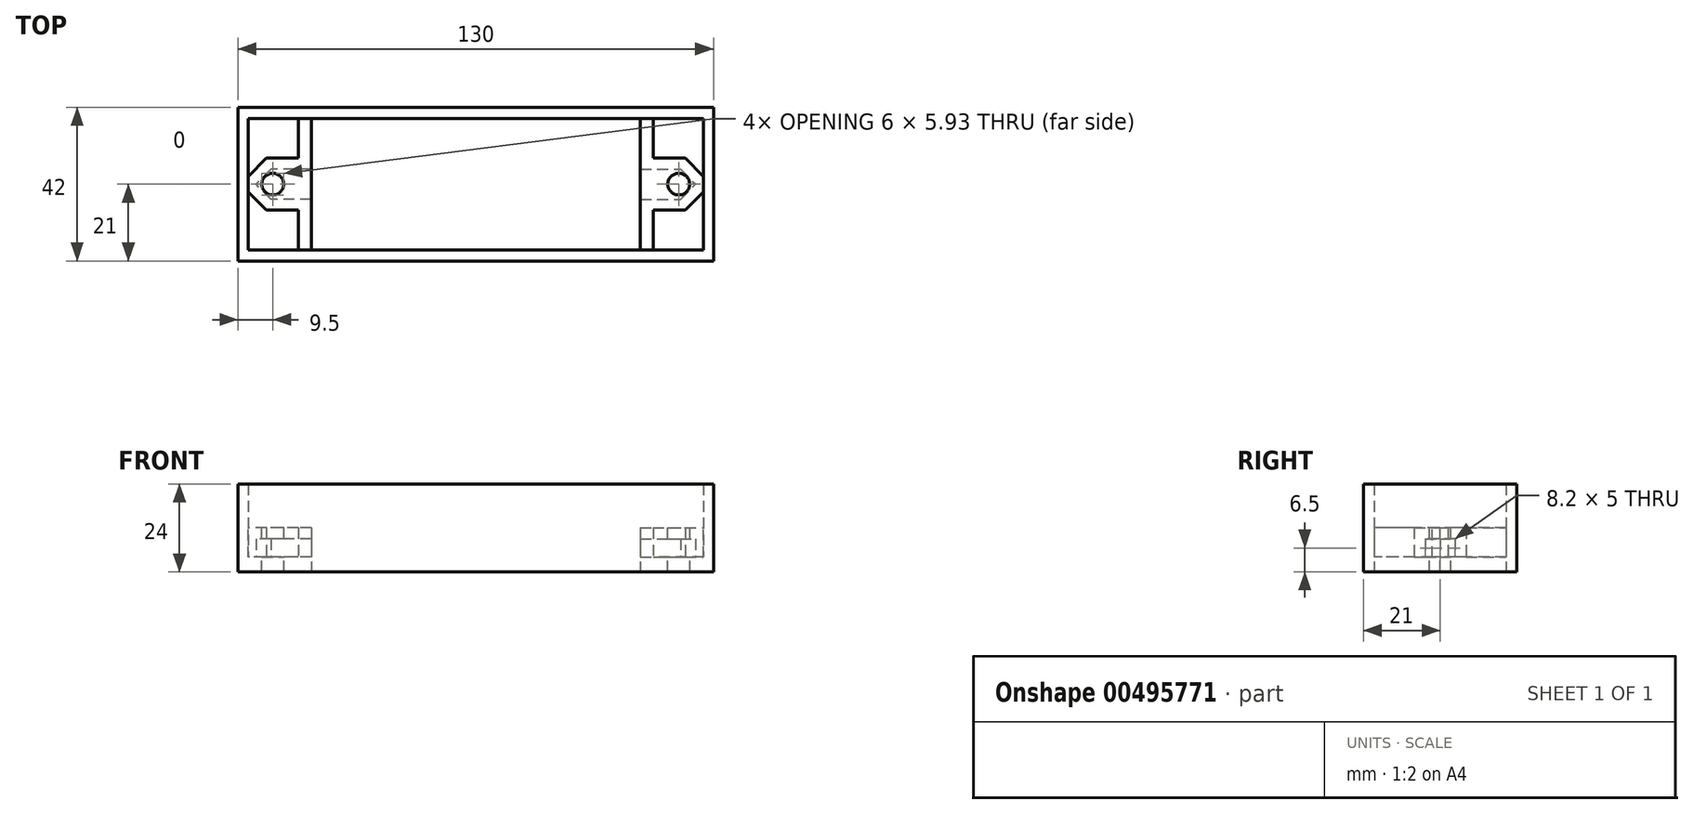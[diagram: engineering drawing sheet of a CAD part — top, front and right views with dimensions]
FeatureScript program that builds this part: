
annotation { "Feature Type Name" : "Feature", "Feature Type Description" : "" }
export const myFeature = defineFeature(function(context is Context, id is Id, definition is map)
    precondition{}
    {
        {
            var Q0;
            Q0=qCreatedBy(makeId("Top.planeOp"),FACE);
            var sketch = newSketch(context, id + "F0", { "sketchPlane" : qUnion([Q0])});
            skLineSegment(sketch, "E0.bottom", {"start": v(65, 21) * mm, "end": v(-65, 21) * mm});
            skLineSegment(sketch, "E0.top", {"start": v(65, -21) * mm, "end": v(-65, -21) * mm});
            skLineSegment(sketch, "E0.left", {"start": v(65, 21) * mm, "end": v(65, -21) * mm});
            skLineSegment(sketch, "E0.right", {"start": v(-65, 21) * mm, "end": v(-65, -21) * mm});
            skPoint(sketch, "E0.middle", {"position": v(0, 0) * mm});
            skLineSegment(sketch, "E1.bottom", {"start": v(-45, 18) * mm, "end": v(45, 18) * mm});
            skLineSegment(sketch, "E1.top", {"start": v(-45, -18) * mm, "end": v(45, -18) * mm});
            skLineSegment(sketch, "E1.left", {"start": v(-45, 18) * mm, "end": v(-45, -18) * mm});
            skLineSegment(sketch, "E1.right", {"start": v(45, 18) * mm, "end": v(45, -18) * mm});
            skSolve(sketch);
        }
        {
            var Q0;
            Q0 = qSketchRegion(id + "F0", true);
            extrude(context, id + "F1", {"entities" : qUnion([Q0]), "depth" : 4 * mm});
        }
        {
            var Q0;
            Q0=makeQuery(id+"F1.opExtrude","CAP_FACE",FACE,{"disambiguationData":[OSD([sQuery(id+"F0.wireOp",EDGE,"E0.bottom"),sQuery(id+"F0.wireOp",EDGE,"E0.top"),sQuery(id+"F0.wireOp",EDGE,"E0.left"),sQuery(id+"F0.wireOp",EDGE,"E0.right"),sQuery(id+"F0.wireOp",EDGE,"E1.bottom"),sQuery(id+"F0.wireOp",EDGE,"E1.top"),sQuery(id+"F0.wireOp",EDGE,"E1.left"),sQuery(id+"F0.wireOp",EDGE,"E1.right")])],"isStart":false});
            var sketch = newSketch(context, id + "F2", { "sketchPlane" : qUnion([Q0])});
            skLineSegment(sketch, "E2", {"start": v(45, 4.1) * mm, "end": v(56, 4.1) * mm});
            skLineSegment(sketch, "E3", {"start": v(56, 4.1) * mm, "end": v(60.1, 0) * mm});
            skLineSegment(sketch, "E4", {"start": v(60.1, 0) * mm, "end": v(45, 0) * mm});
            skLineSegment(sketch, "E5", {"start": v(45, 0) * mm, "end": v(45, 4.1) * mm});
            skLineSegment(sketch, "E6", {"start": v(56, 21) * mm, "end": v(56, -21) * mm, "construction": true});
            skLineSegment(sketch, "E7.MirrorCS", {"start": v(45, -4.1) * mm, "end": v(56, -4.1) * mm});
            skLineSegment(sketch, "E8.MirrorCS", {"start": v(56, -4.1) * mm, "end": v(60.1, 0) * mm});
            skLineSegment(sketch, "E9.MirrorCS", {"start": v(45, 0) * mm, "end": v(45, -4.1) * mm});
            skLineSegment(sketch, "E10.0", {"start": v(45, -7.1) * mm, "end": v(57.24, -7.1) * mm});
            skLineSegment(sketch, "E10.1", {"start": v(57.24, -7.1) * mm, "end": v(64.34, 0) * mm});
            skLineSegment(sketch, "E10.2", {"start": v(57.24, 7.1) * mm, "end": v(64.34, 0) * mm});
            skLineSegment(sketch, "E10.3", {"start": v(45, 7.1) * mm, "end": v(57.24, 7.1) * mm});
            skLineSegment(sketch, "E11.0", {"start": v(-60, -16) * mm, "end": v(60, -16) * mm, "construction": true});
            skLineSegment(sketch, "E11.1", {"start": v(-60, 16) * mm, "end": v(-60, -16) * mm, "construction": true});
            skLineSegment(sketch, "E11.2", {"start": v(60, 16) * mm, "end": v(-60, 16) * mm, "construction": true});
            skLineSegment(sketch, "E11.3", {"start": v(60, -16) * mm, "end": v(60, 16) * mm, "construction": true});
            skLineSegment(sketch, "E12.0", {"start": v(65, 21) * mm, "end": v(-60, 21) * mm});
            skLineSegment(sketch, "E12.1", {"start": v(65, -16) * mm, "end": v(65, 21) * mm});
            skSolve(sketch);
        }
        {
            var Q0;
            {var subQ1=sQuery(id+"F2.wireOp",EDGE,"E7.MirrorCS");Q0=makeQuery(id+"F2.imprint","IMPRINT",FACE,{"disambiguationData":[TD([[makeQuery(id+"F2.imprint","IMPRINT",EDGE,{"derivedFrom":subQ1}),-1.0]])]});}
            extrude(context, id + "F3", {"entities" : qUnion([Q0]), "operationType" : NewBodyOperationType.ADD, "depth" : 5 * mm});
        }
        {
            var Q0;
            Q0=makeQuery(id+"F3.opExtrude","CAP_FACE",FACE,{"disambiguationData":[OSD([sQuery(id+"F0.wireOp",EDGE,"E1.right"),sQuery(id+"F2.wireOp",EDGE,"E7.MirrorCS"),sQuery(id+"F2.wireOp",EDGE,"E8.MirrorCS"),sQuery(id+"F2.wireOp",EDGE,"E3"),sQuery(id+"F2.wireOp",EDGE,"E2"),sQuery(id+"F2.wireOp",EDGE,"E10.0"),sQuery(id+"F2.wireOp",EDGE,"E10.1"),sQuery(id+"F2.wireOp",EDGE,"E10.2"),sQuery(id+"F2.wireOp",EDGE,"E10.3")])],"isStart":false});
            var sketch = newSketch(context, id + "F4", { "sketchPlane" : qUnion([Q0])});
            skLineSegment(sketch, "E13", {"start": v(45, 7.1) * mm, "end": v(45, -7.1) * mm});
            skLineSegment(sketch, "E14", {"start": v(45, -7.1) * mm, "end": v(57.24, -7.1) * mm});
            skLineSegment(sketch, "E15", {"start": v(57.24, -7.1) * mm, "end": v(64.34, 0) * mm});
            skLineSegment(sketch, "E16", {"start": v(64.34, 0) * mm, "end": v(57.24, 7.1) * mm});
            skLineSegment(sketch, "E17", {"start": v(57.24, 7.1) * mm, "end": v(45, 7.1) * mm});
            skSolve(sketch);
        }
        {
            var Q0;
            {var subQ0=sQuery(id+"F4.wireOp",EDGE,"E14");Q0=makeQuery(id+"F4.imprint","IMPRINT",FACE,{"disambiguationData":[TD([[makeQuery(id+"F4.imprint","IMPRINT",EDGE,{"derivedFrom":subQ0}),1.0]])]});}
            var Q1;
            {var subQ0=makeQuery(id+"F3.opExtrude","CAP_EDGE",EDGE,{"disambiguationData":[OSD([sQuery(id+"F2.wireOp",EDGE,"E7.MirrorCS")])],"isStart":false});Q1=makeQuery(id+"F4.imprint","IMPRINT",FACE,{"disambiguationData":[TD([[makeQuery(id+"F4.imprint","IMPRINT",EDGE,{"derivedFrom":subQ0}),1.0]])]});}
            extrude(context, id + "F5", {"entities" : qUnion([Q0, Q1]), "operationType" : NewBodyOperationType.ADD, "depth" : 3 * mm});
        }
        {
            var Q0;
            Q0=makeQuery(id+"F5.boolean.opBoolean","MERGE",EDGE,{"derivedFrom":[makeQuery(id+"F3.opExtrude","SWEPT_EDGE",EDGE,{"disambiguationData":[OSD([sQuery(id+"F2.wireOp",EDGE,"E10.1"),sQuery(id+"F2.wireOp",EDGE,"E10.2")])]}),makeQuery(id+"F5.opExtrude","SWEPT_EDGE",EDGE,{"disambiguationData":[OSD([sQuery(id+"F4.wireOp",EDGE,"E15"),sQuery(id+"F4.wireOp",EDGE,"E16")])]})]});
            chamfer(context, id + "F6", {"entities" : qUnion([Q0]), "width" : 3 * mm, "tangentPropagation" : true});
        }
        {
            var Q0;
            {var subQ0=sQuery(id+"F2.wireOp",EDGE,"E7.MirrorCS");var subQ1=sQuery(id+"F0.wireOp",EDGE,"E1.right");Q0=makeQuery(id+"F3.boolean.opBoolean","SPLIT",FACE,{"disambiguationData":[TD([makeQuery(id+"F3.opExtrude","SWEPT_FACE",FACE,{"disambiguationData":[OSD([subQ0])]})])],"derivedFrom":makeQuery(id+"F1.opExtrude","CAP_FACE",FACE,{"disambiguationData":[OSD([sQuery(id+"F0.wireOp",EDGE,"E0.bottom"),sQuery(id+"F0.wireOp",EDGE,"E0.top"),sQuery(id+"F0.wireOp",EDGE,"E0.left"),sQuery(id+"F0.wireOp",EDGE,"E0.right"),sQuery(id+"F0.wireOp",EDGE,"E1.bottom"),sQuery(id+"F0.wireOp",EDGE,"E1.top"),sQuery(id+"F0.wireOp",EDGE,"E1.left"),subQ1])],"isStart":false})});}
            var sketch = newSketch(context, id + "F7", { "sketchPlane" : qUnion([Q0])});
            skLineSegment(sketch, "E18", {"start": v(55.5, 6.12) * mm, "end": v(55.5, -6.06) * mm, "construction": true});
            skCircle(sketch, "E19", {"center": v(55.5, 0.03) * mm, "radius": 3 * mm});
            skSolve(sketch);
        }
        {
            var Q0;
            Q0 = qSketchRegion(id + "F7", true);
            extrude(context, id + "F8", {"entities" : qUnion([Q0]), "operationType" : NewBodyOperationType.REMOVE, "endBound" : BoundingType.SYMMETRIC, "oppositeDirection" : true, "depth" : 25 * mm});
        }
        {
            var Q0;
            Q0=makeQuery(id+"F1.opExtrude","SWEPT_BODY",BODY,{"disambiguationData":[OSD([sQuery(id+"F0.wireOp",EDGE,"E0.bottom"),sQuery(id+"F0.wireOp",EDGE,"E0.top"),sQuery(id+"F0.wireOp",EDGE,"E0.left"),sQuery(id+"F0.wireOp",EDGE,"E0.right"),sQuery(id+"F0.wireOp",EDGE,"E1.bottom"),sQuery(id+"F0.wireOp",EDGE,"E1.top"),sQuery(id+"F0.wireOp",EDGE,"E1.left"),sQuery(id+"F0.wireOp",EDGE,"E1.right")])]});
            var Q1;
            Q1=qCreatedBy(makeId("Right.planeOp"),FACE);
            mirror(context, id + "F9", {"operationType" : NewBodyOperationType.ADD, "entities" : qUnion([Q0]), "mirrorPlane" : qUnion([Q1])});
        }
        {
            var Q0;
            Q0=makeQuery(id+"F9.opPattern","COPY",FACE,{"derivedFrom":makeQuery(id+"F5.opExtrude","CAP_FACE",FACE,{"disambiguationData":[OSD([sQuery(id+"F4.wireOp",EDGE,"E13"),sQuery(id+"F4.wireOp",EDGE,"E14"),sQuery(id+"F4.wireOp",EDGE,"E15"),sQuery(id+"F4.wireOp",EDGE,"E16"),sQuery(id+"F4.wireOp",EDGE,"E17")])],"isStart":false}),"instanceName":"1"});
            var sketch = newSketch(context, id + "F10", { "sketchPlane" : qUnion([Q0])});
            skCircle(sketch, "E20", {"center": v(-55.5, 0.03) * mm, "radius": 3 * mm});
            skCircle(sketch, "E21.MirrorC", {"center": v(55.5, 0.03) * mm, "radius": 3 * mm});
            skSolve(sketch);
        }
        {
            var Q0;
            Q0 = qSketchRegion(id + "F10", true);
            extrude(context, id + "F11", {"entities" : qUnion([Q0]), "operationType" : NewBodyOperationType.REMOVE, "oppositeDirection" : true, "depth" : 37.9 * mm});
        }
        {
            var Q0;
            {var subQ5=sQuery(id+"F0.wireOp",EDGE,"E1.right");var subQ20=sQuery(id+"F0.wireOp",EDGE,"E0.left");var subQ22=sQuery(id+"F0.wireOp",EDGE,"E0.top");var subQ24=sQuery(id+"F0.wireOp",EDGE,"E0.right");var subQ27=sQuery(id+"F0.wireOp",EDGE,"E0.bottom");var subQ28=makeQuery(id+"F1.opExtrude","SWEPT_FACE",FACE,{"disambiguationData":[OSD([subQ27])]});var subQ29=sQuery(id+"F0.wireOp",EDGE,"E1.bottom");var subQ31=sQuery(id+"F0.wireOp",EDGE,"E1.top");var subQ33=sQuery(id+"F0.wireOp",EDGE,"E1.left");Q0=makeQuery(id+"F9.boolean.opBoolean","SPLIT",FACE,{"disambiguationData":[TD([subQ28])],"derivedFrom":makeQuery(id+"F3.boolean.opBoolean","SPLIT",FACE,{"disambiguationData":[TD([subQ28])],"derivedFrom":makeQuery(id+"F1.opExtrude","CAP_FACE",FACE,{"disambiguationData":[OSD([subQ27,subQ22,subQ20,subQ24,subQ29,subQ31,subQ33,subQ5])],"isStart":false})})});}
            var sketch = newSketch(context, id + "F12", { "sketchPlane" : qUnion([Q0])});
            skLineSegment(sketch, "E22.bottom", {"start": v(62.22, 18) * mm, "end": v(-62.22, 18) * mm});
            skLineSegment(sketch, "E22.top", {"start": v(62.22, -18) * mm, "end": v(-62.22, -18) * mm});
            skLineSegment(sketch, "E22.left", {"start": v(62.22, 18) * mm, "end": v(62.22, -18) * mm});
            skLineSegment(sketch, "E22.right", {"start": v(-62.22, 18) * mm, "end": v(-62.22, -18) * mm});
            skPoint(sketch, "E22.middle", {"position": v(0, 0) * mm});
            skLineSegment(sketch, "E23.bottom", {"start": v(65, 21) * mm, "end": v(-65, 21) * mm});
            skLineSegment(sketch, "E23.top", {"start": v(65, -21) * mm, "end": v(-65, -21) * mm});
            skLineSegment(sketch, "E23.left", {"start": v(65, 21) * mm, "end": v(65, -21) * mm});
            skLineSegment(sketch, "E23.right", {"start": v(-65, 21) * mm, "end": v(-65, -21) * mm});
            skSolve(sketch);
        }
        {
            var Q0;
            Q0=makeQuery(id+"F12.imprint","IMPRINT",FACE,{"disambiguationData":[TD([[makeQuery(id+"F12.imprint","IMPRINT",EDGE,{"derivedFrom":sQuery(id+"F12.wireOp",EDGE,"E23.bottom")}),1.0]])]});
            extrude(context, id + "F13", {"entities" : qUnion([Q0]), "operationType" : NewBodyOperationType.ADD, "depth" : 20 * mm});
        }
        {
            var Q0;
            {var subQ1=sQuery(id+"F0.wireOp",EDGE,"E1.right");var subQ5=sQuery(id+"F2.wireOp",EDGE,"E10.3");var subQ9=sQuery(id+"F0.wireOp",EDGE,"E1.left");var subQ11=makeQuery(id+"F5.opExtrude","SWEPT_FACE",FACE,{"disambiguationData":[OSD([sQuery(id+"F4.wireOp",EDGE,"E17")])]});var subQ12=makeQuery(id+"F3.opExtrude","SWEPT_FACE",FACE,{"disambiguationData":[OSD([subQ5])]});var subQ13=makeQuery(id+"F9.opPattern","COPY",FACE,{"derivedFrom":makeQuery(id+"F5.boolean.opBoolean","MERGE",FACE,{"derivedFrom":[subQ12,subQ11]}),"instanceName":"1"});var subQ14=sQuery(id+"F0.wireOp",EDGE,"E1.bottom");var subQ28=sQuery(id+"F0.wireOp",EDGE,"E0.left");var subQ30=sQuery(id+"F0.wireOp",EDGE,"E0.top");var subQ32=sQuery(id+"F0.wireOp",EDGE,"E0.right");var subQ34=sQuery(id+"F0.wireOp",EDGE,"E0.bottom");var subQ35=makeQuery(id+"F1.opExtrude","SWEPT_FACE",FACE,{"disambiguationData":[OSD([subQ34])]});var subQ36=sQuery(id+"F0.wireOp",EDGE,"E1.top");Q0=makeQuery(id+"F13.boolean.opBoolean","SPLIT",FACE,{"disambiguationData":[TD([subQ13])],"derivedFrom":makeQuery(id+"F9.boolean.opBoolean","SPLIT",FACE,{"disambiguationData":[TD([subQ35])],"derivedFrom":makeQuery(id+"F3.boolean.opBoolean","SPLIT",FACE,{"disambiguationData":[TD([subQ35])],"derivedFrom":makeQuery(id+"F1.opExtrude","CAP_FACE",FACE,{"disambiguationData":[OSD([subQ34,subQ30,subQ28,subQ32,subQ14,subQ36,subQ9,subQ1])],"isStart":false})})})});}
            var sketch = newSketch(context, id + "F14", { "sketchPlane" : qUnion([Q0])});
            skLineSegment(sketch, "E24.bottom", {"start": v(-45, 7.1) * mm, "end": v(-48.5, 7.1) * mm});
            skLineSegment(sketch, "E24.top", {"start": v(-45, 18) * mm, "end": v(-48.5, 18) * mm});
            skLineSegment(sketch, "E24.left", {"start": v(-45, 7.1) * mm, "end": v(-45, 18) * mm});
            skLineSegment(sketch, "E24.right", {"start": v(-48.5, 7.1) * mm, "end": v(-48.5, 18) * mm});
            skSolve(sketch);
        }
        {
            var Q0;
            Q0 = qSketchRegion(id + "F14", true);
            extrude(context, id + "F15", {"entities" : qUnion([Q0]), "operationType" : NewBodyOperationType.ADD, "depth" : 8 * mm});
        }
        {
            var Q0;
            Q0=makeQuery(id+"F1.opExtrude","SWEPT_BODY",BODY,{"disambiguationData":[OSD([sQuery(id+"F0.wireOp",EDGE,"E0.bottom"),sQuery(id+"F0.wireOp",EDGE,"E0.top"),sQuery(id+"F0.wireOp",EDGE,"E0.left"),sQuery(id+"F0.wireOp",EDGE,"E0.right"),sQuery(id+"F0.wireOp",EDGE,"E1.bottom"),sQuery(id+"F0.wireOp",EDGE,"E1.top"),sQuery(id+"F0.wireOp",EDGE,"E1.left"),sQuery(id+"F0.wireOp",EDGE,"E1.right")])]});
            var Q1;
            Q1=qCreatedBy(makeId("Front.planeOp"),FACE);
            mirror(context, id + "F16", {"operationType" : NewBodyOperationType.ADD, "entities" : qUnion([Q0]), "mirrorPlane" : qUnion([Q1])});
        }
        {
            var Q0;
            Q0=makeQuery(id+"F1.opExtrude","SWEPT_BODY",BODY,{"disambiguationData":[OSD([sQuery(id+"F0.wireOp",EDGE,"E0.bottom"),sQuery(id+"F0.wireOp",EDGE,"E0.top"),sQuery(id+"F0.wireOp",EDGE,"E0.left"),sQuery(id+"F0.wireOp",EDGE,"E0.right"),sQuery(id+"F0.wireOp",EDGE,"E1.bottom"),sQuery(id+"F0.wireOp",EDGE,"E1.top"),sQuery(id+"F0.wireOp",EDGE,"E1.left"),sQuery(id+"F0.wireOp",EDGE,"E1.right")])]});
            var Q1;
            Q1=qCreatedBy(makeId("Right.planeOp"),FACE);
            mirror(context, id + "F17", {"operationType" : NewBodyOperationType.ADD, "entities" : qUnion([Q0]), "mirrorPlane" : qUnion([Q1])});
        }
    });
